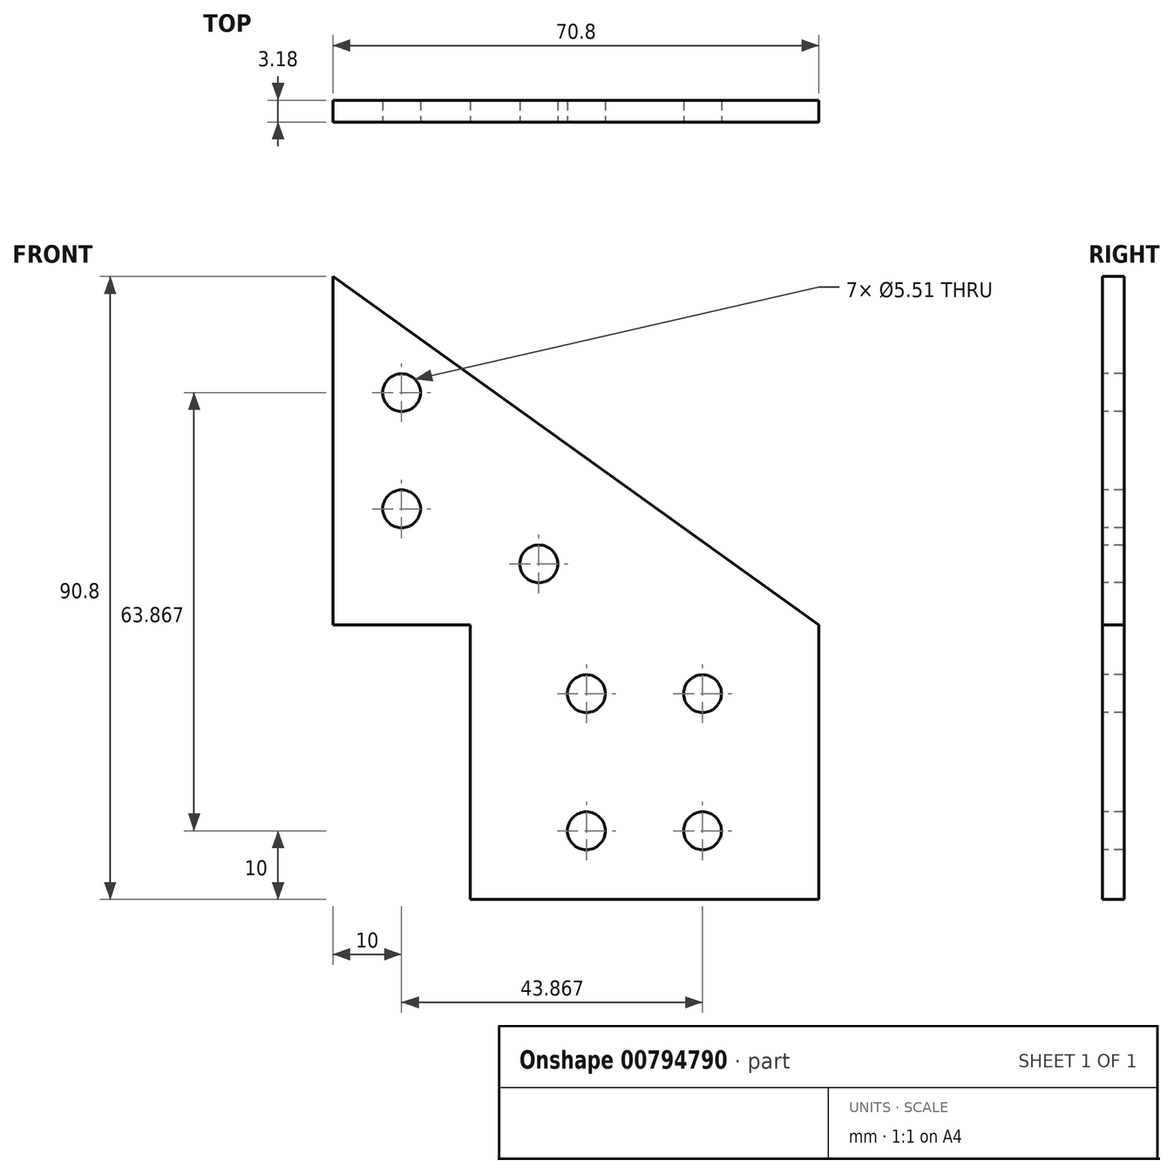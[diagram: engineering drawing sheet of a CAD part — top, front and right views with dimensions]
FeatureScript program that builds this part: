
annotation { "Feature Type Name" : "Feature", "Feature Type Description" : "" }
export const myFeature = defineFeature(function(context is Context, id is Id, definition is map)
    precondition{}
    {
        {
            var Q0;
            Q0=qCreatedBy(makeId("Front.planeOp"),FACE);
            var sketch = newSketch(context, id + "F0", { "sketchPlane" : qUnion([Q0])});
            skLineSegment(sketch, "E0.top", {"start": v(0, -40) * mm, "end": v(50.8, -40) * mm});
            skLineSegment(sketch, "E0.left", {"start": v(0, -14.51) * mm, "end": v(0, -40) * mm});
            skLineSegment(sketch, "E0.right", {"start": v(50.8, 0) * mm, "end": v(50.8, -40) * mm});
            skLineSegment(sketch, "E1", {"start": v(-20, 0) * mm, "end": v(-20, 50.8) * mm});
            skLineSegment(sketch, "E2", {"start": v(-20, 0) * mm, "end": v(0, 0) * mm});
            skLineSegment(sketch, "E3", {"start": v(0, 0) * mm, "end": v(0, -14.51) * mm});
            skPoint(sketch, "E4.positionSnap0", {"position": v(25.4, -40) * mm});
            skPoint(sketch, "E5", {"position": v(16.93, -40) * mm});
            skPoint(sketch, "E6", {"position": v(33.87, -40) * mm});
            skPoint(sketch, "E7", {"position": v(33.87, -30) * mm});
            skPoint(sketch, "E8", {"position": v(16.93, -30) * mm});
            skPoint(sketch, "E9", {"position": v(16.93, -10) * mm});
            skPoint(sketch, "E10", {"position": v(33.87, -10) * mm});
            skLineSegment(sketch, "E11", {"start": v(-20, 50.8) * mm, "end": v(50.8, 0) * mm});
            skPoint(sketch, "E12", {"position": v(-10, 0) * mm});
            skPoint(sketch, "E13", {"position": v(-10, 33.87) * mm});
            skPoint(sketch, "E14", {"position": v(-10, 16.93) * mm});
            skPoint(sketch, "E15", {"position": v(10, 8.9) * mm});
            skCircle(sketch, "E16", {"center": v(-10, 33.87) * mm, "radius": 2.76 * mm});
            skCircle(sketch, "E17", {"center": v(-10, 16.93) * mm, "radius": 2.76 * mm});
            skCircle(sketch, "E18", {"center": v(10, 8.9) * mm, "radius": 2.76 * mm});
            skCircle(sketch, "E19", {"center": v(16.93, -10) * mm, "radius": 2.76 * mm});
            skCircle(sketch, "E20", {"center": v(33.87, -10) * mm, "radius": 2.76 * mm});
            skCircle(sketch, "E21", {"center": v(16.93, -30) * mm, "radius": 2.76 * mm});
            skCircle(sketch, "E22", {"center": v(33.87, -30) * mm, "radius": 2.76 * mm});
            skSolve(sketch);
        }
        {
            var Q0;
            Q0=makeQuery(id+"F0.imprint","IMPRINT",FACE,{"disambiguationData":[TD([[makeQuery(id+"F0.imprint","IMPRINT",EDGE,{"derivedFrom":sQuery(id+"F0.wireOp",EDGE,"E0.top")}),1.0]])]});
            var Q1;
            {var subQ1=sQuery(id+"F0.wireOp",EDGE,"E1");Q1=makeQuery(id+"F0.imprint","IMPRINT",FACE,{"disambiguationData":[TD([[makeQuery(id+"F0.imprint","IMPRINT",EDGE,{"derivedFrom":subQ1}),-1.0]])]});}
            extrude(context, id + "F1", {"entities" : qUnion([Q0, Q1]), "oppositeDirection" : true, "depth" : 3.17 * mm, "offsetDistance" : 25.4 * mm});
        }
    });
